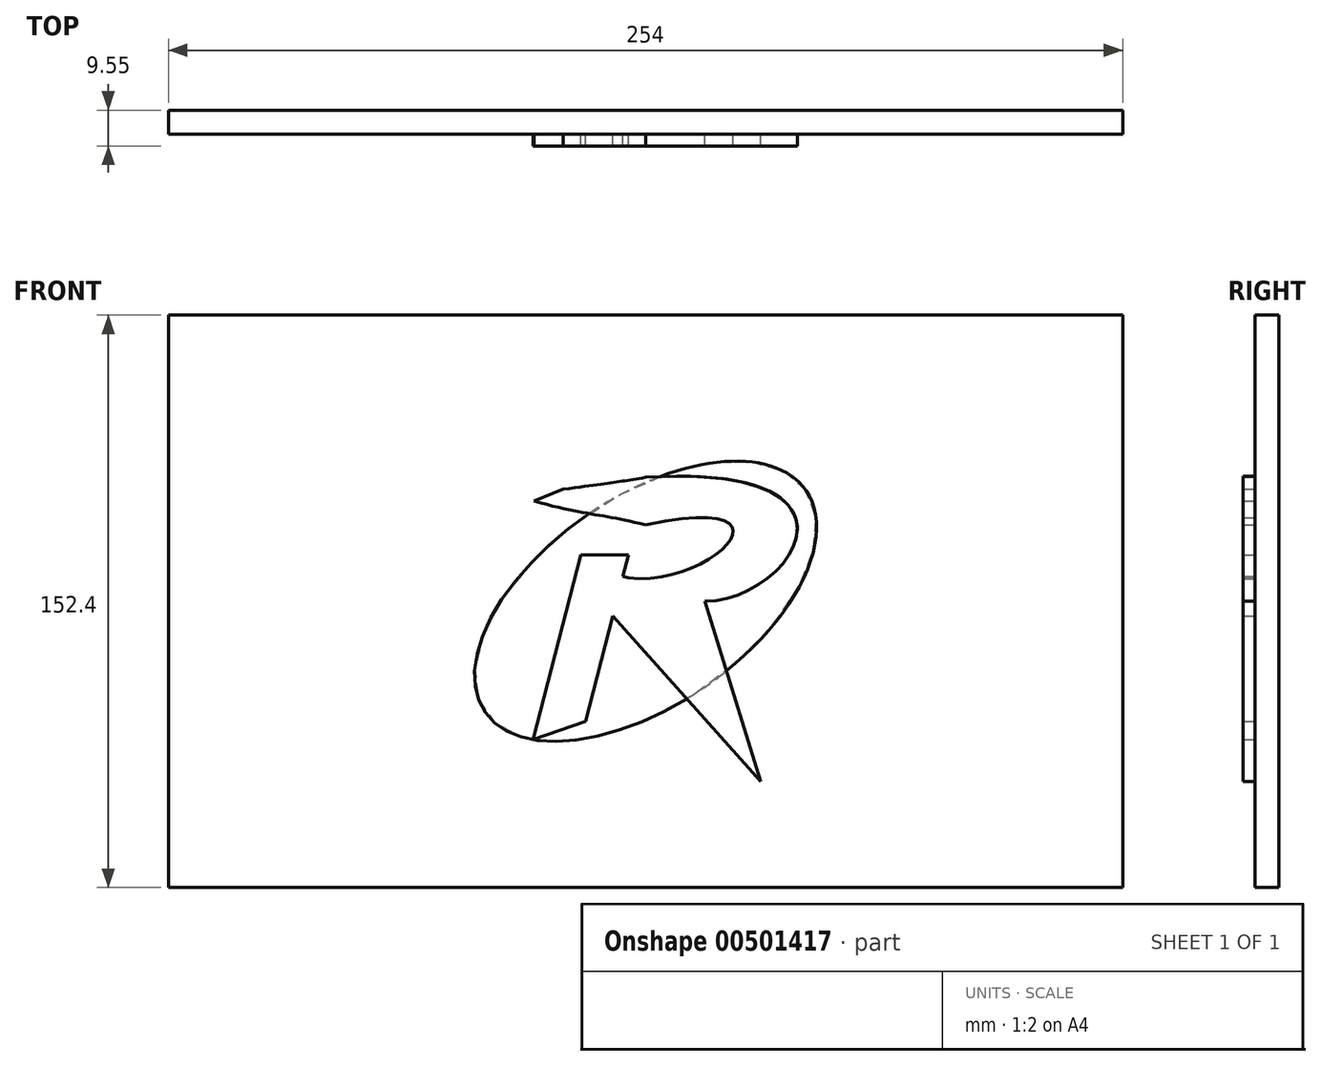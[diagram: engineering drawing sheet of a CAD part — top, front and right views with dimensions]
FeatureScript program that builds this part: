
annotation { "Feature Type Name" : "Feature", "Feature Type Description" : "" }
export const myFeature = defineFeature(function(context is Context, id is Id, definition is map)
    precondition{}
    {
        {
            var Q0;
            Q0=qCreatedBy(makeId("Front.planeOp"),FACE);
            var sketch = newSketch(context, id + "F0", { "sketchPlane" : qUnion([Q0])});
            skLineSegment(sketch, "E0.bottom", {"start": v(127, 76.2) * mm, "end": v(-127, 76.2) * mm});
            skLineSegment(sketch, "E0.top", {"start": v(127, -76.2) * mm, "end": v(-127, -76.2) * mm});
            skLineSegment(sketch, "E0.left", {"start": v(127, 76.2) * mm, "end": v(127, -76.2) * mm});
            skLineSegment(sketch, "E0.right", {"start": v(-127, 76.2) * mm, "end": v(-127, -76.2) * mm});
            skPoint(sketch, "E0.middle", {"position": v(0, 0) * mm});
            skSolve(sketch);
        }
        {
            var Q0;
            Q0 = qSketchRegion(id + "F0", true);
            extrude(context, id + "F1", {"entities" : qUnion([Q0]), "oppositeDirection" : true, "depth" : 6.35 * mm});
        }
        {
            var Q0;
            Q0=makeQuery(id+"F1.opExtrude","CAP_FACE",FACE,{"disambiguationData":[OSD([sQuery(id+"F0.wireOp",EDGE,"E0.bottom"),sQuery(id+"F0.wireOp",EDGE,"E0.top"),sQuery(id+"F0.wireOp",EDGE,"E0.left"),sQuery(id+"F0.wireOp",EDGE,"E0.right")])],"isStart":true});
            var sketch = newSketch(context, id + "F2", { "sketchPlane" : qUnion([Q0])});
            skEllipse(sketch, "E1", {"center": v(0, 0) * mm, "majorRadius": 51.93 * mm, "minorRadius": 27.74 * mm, "majorAxis": v(0.82, 0.57)});
            skSolve(sketch);
        }
        {
            var Q0;
            Q0 = qSketchRegion(id + "F2", true);
            extrude(context, id + "F3", {"entities" : qUnion([Q0]), "depth" : 0.03 * mm});
        }
        {
            var Q0;
            Q0=makeQuery(id+"F3.opExtrude","CAP_FACE",FACE,{"disambiguationData":[OSD([sQuery(id+"F2.wireOp",EDGE,"E1")])],"isStart":false});
            var sketch = newSketch(context, id + "F4", { "sketchPlane" : qUnion([Q0])});
            skLineSegment(sketch, "E2", {"start": v(-29.94, -36.85) * mm, "end": v(-17.24, 12.33) * mm});
            skLineSegment(sketch, "E3", {"start": v(-17.24, 12.33) * mm, "end": v(-4.54, 12.33) * mm});
            skPoint(sketch, "E4.start.orphan", {"position": v(-4.54, 6.2) * mm});
            skLineSegment(sketch, "E5", {"start": v(-4.54, 12.33) * mm, "end": v(-15.97, -31.93) * mm});
            skLineSegment(sketch, "E6", {"start": v(-15.97, -31.93) * mm, "end": v(-29.94, -36.85) * mm});
            skLineSegment(sketch, "E7", {"start": v(-8.73, -3.9) * mm, "end": v(30.6, -47.95) * mm});
            skLineSegment(sketch, "E8", {"start": v(30.6, -47.95) * mm, "end": v(15.78, 0) * mm});
            skPoint(sketch, "E8.endSnap0", {"position": v(15.78, -22.82) * mm});
            skPoint(sketch, "E9.1.internal.orphan", {"position": v(26.1, 2.97) * mm});
            skLineSegment(sketch, "E10", {"start": v(-4.54, 6.2) * mm, "end": v(-6.03, 6.59) * mm});
            skLineSegment(sketch, "E11", {"start": v(0, 33.02) * mm, "end": v(0, 20.32) * mm});
            skFitSpline(sketch, "E12", {"points": [v(-21.9, 29.85) * mm, v(0, 33.02) * mm], "startDerivative": vector(37.31, 4.94) * mm, "endDerivative": vector(20.72, 3.68) * mm});
            skFitSpline(sketch, "E13", {"points": [v(-29.71, 26.67) * mm, v(0, 20.32) * mm], "startDerivative": vector(41.8, -11.55) * mm, "endDerivative": vector(34.96, -9.03) * mm});
            skLineSegment(sketch, "E14", {"start": v(-21.9, 29.85) * mm, "end": v(-29.71, 26.67) * mm});
            skPoint(sketch, "E15.startDerivative.orphan", {"position": v(0, 2.5) * mm});
            skPoint(sketch, "E16.endDerivative.orphan", {"position": v(20.42, 2.97) * mm});
            skFitSpline(sketch, "E17", {"points": [v(0, 33.02) * mm, v(15.78, 0) * mm], "startDerivative": vector(190.76, 11.73) * mm, "endDerivative": vector(-68.46, 0) * mm});
            skFitSpline(sketch, "E18", {"points": [v(0, 20.32) * mm, v(-4.54, 6.2) * mm], "startDerivative": vector(128.13, 27.64) * mm, "endDerivative": vector(-67.58, 7.74) * mm});
            skSolve(sketch);
        }
        {
            var Q0;
            Q0=makeQuery(id+"F4.imprint","IMPRINT",FACE,{"disambiguationData":[TD([[makeQuery(id+"F4.imprint","IMPRINT",EDGE,{"derivedFrom":sQuery(id+"F4.wireOp",EDGE,"1bMEApZZ-89pQ-8x88-L1T0-ttb1f4Nbn45I")}),1.0]])]});
            var Q1;
            {var subQ11=sQuery(id+"F4.wireOp",EDGE,"E15");Q1=makeQuery(id+"F4.imprint","IMPRINT",FACE,{"disambiguationData":[TD([[makeQuery(id+"F4.imprint","IMPRINT",EDGE,{"derivedFrom":subQ11}),-1.0]])]});}
            var Q2;
            {var subQ0=sQuery(id+"F4.wireOp",EDGE,"E8");var subQ1=sQuery(id+"F4.wireOp",EDGE,"E7");var subQ2=makeQuery(id+"F4.imprint","INTERSECT",VERTEX,{"derivedFrom":[subQ1,subQ0]});Q2=makeQuery(id+"F4.imprint","IMPRINT",FACE,{"disambiguationData":[TD([[makeQuery(id+"F4.imprint","IMPRINT",EDGE,{"disambiguationData":[TD([[subQ2,1.0]])],"derivedFrom":subQ1}),1.0]])]});}
            var Q3;
            {var subQ0=sQuery(id+"F4.wireOp",EDGE,"E11");Q3=makeQuery(id+"F4.imprint","IMPRINT",FACE,{"disambiguationData":[TD([[makeQuery(id+"F4.imprint","IMPRINT",EDGE,{"derivedFrom":subQ0}),1.0]])]});}
            var Q4;
            Q4=makeQuery(id+"F4.imprint","IMPRINT",FACE,{"disambiguationData":[TD([[makeQuery(id+"F4.imprint","IMPRINT",EDGE,{"derivedFrom":sQuery(id+"F4.wireOp",EDGE,"E2")}),-1.0]])]});
            var Q5;
            {var subQ0=sQuery(id+"F4.wireOp",EDGE,"E10");Q5=makeQuery(id+"F4.imprint","IMPRINT",FACE,{"disambiguationData":[TD([[makeQuery(id+"F4.imprint","IMPRINT",EDGE,{"derivedFrom":subQ0}),1.0]])]});}
            var Q6;
            {var subQ0=sQuery(id+"F4.wireOp",EDGE,"E13");var subQ3=makeQuery(id+"F3.opExtrude","CAP_EDGE",EDGE,{"disambiguationData":[OSD([sQuery(id+"F2.wireOp",EDGE,"E1")])],"isStart":false});var subQ5=makeQuery(id+"F4.imprint","INTERSECT",VERTEX,{"derivedFrom":[subQ3,subQ0]});Q6=makeQuery(id+"F4.imprint","IMPRINT",FACE,{"disambiguationData":[TD([[makeQuery(id+"F4.imprint","IMPRINT",EDGE,{"disambiguationData":[TD([[subQ5,1.0]])],"derivedFrom":subQ3}),1.0]])]});}
            var Q7;
            {var subQ4=sQuery(id+"F4.wireOp",EDGE,"E12");Q7=makeQuery(id+"F4.imprint","IMPRINT",FACE,{"disambiguationData":[TD([[makeQuery(id+"F4.imprint","IMPRINT",EDGE,{"derivedFrom":subQ4}),-1.0]])]});}
            extrude(context, id + "F5", {"entities" : qUnion([Q0, Q1, Q2, Q3, Q4, Q5, Q6, Q7]), "depth" : 3.17 * mm});
        }
    });
